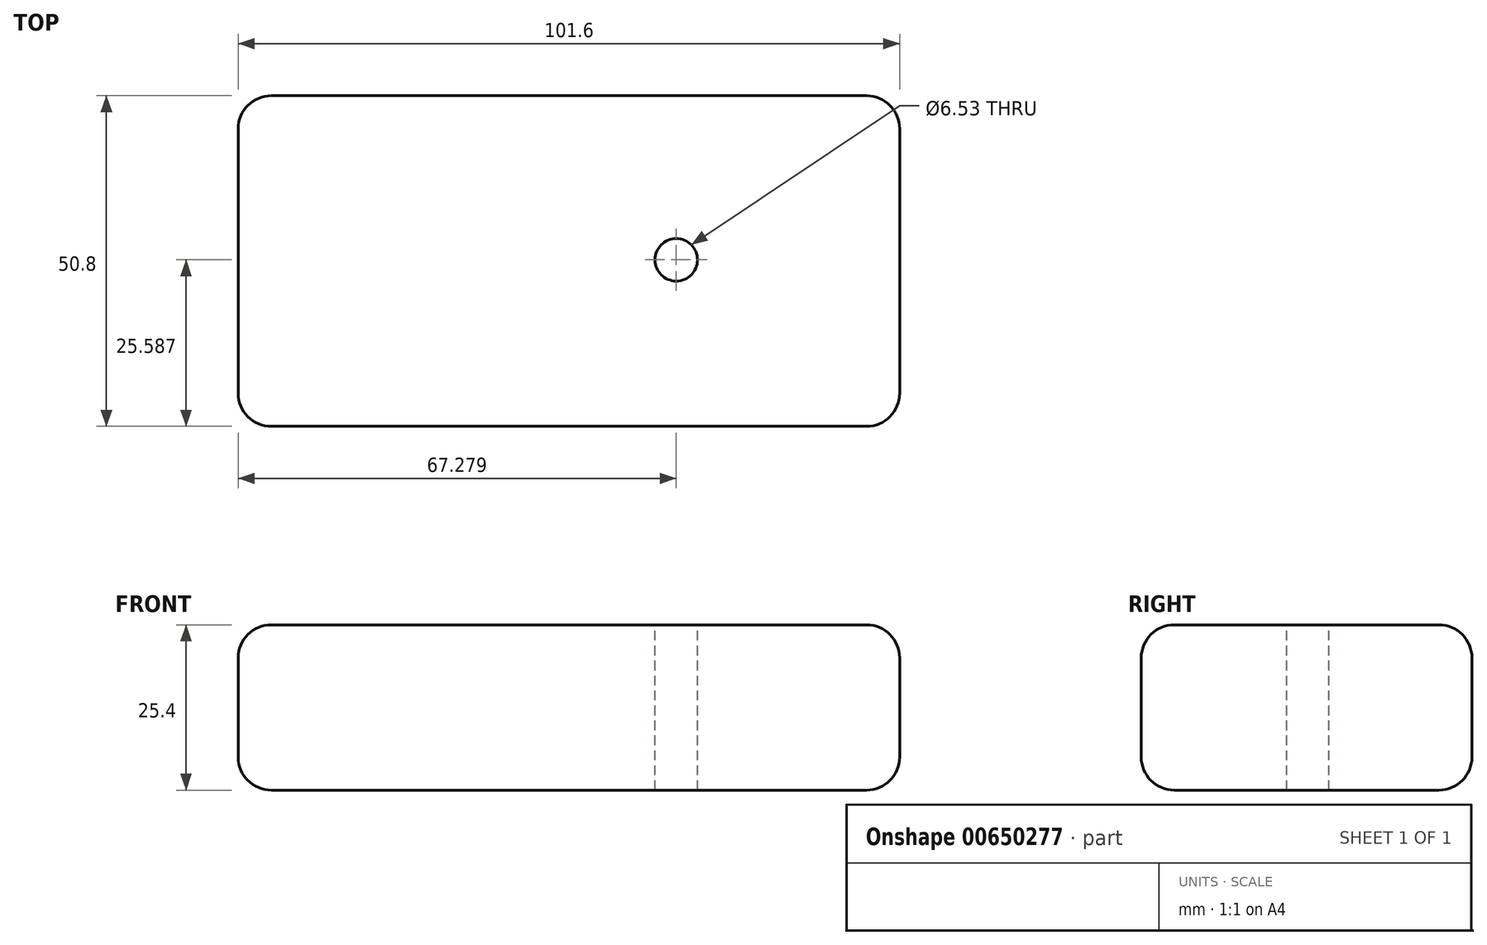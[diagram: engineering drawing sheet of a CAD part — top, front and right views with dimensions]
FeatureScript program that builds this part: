
annotation { "Feature Type Name" : "Feature", "Feature Type Description" : "" }
export const myFeature = defineFeature(function(context is Context, id is Id, definition is map)
    precondition{}
    {
        {
            var Q0;
            Q0=qCreatedBy(makeId("Top.planeOp"),FACE);
            var sketch = newSketch(context, id + "F0", { "sketchPlane" : qUnion([Q0])});
            skLineSegment(sketch, "E0.bottom", {"start": v(0, 50.8) * mm, "end": v(101.6, 50.8) * mm});
            skLineSegment(sketch, "E0.top", {"start": v(0, 0) * mm, "end": v(101.6, 0) * mm});
            skLineSegment(sketch, "E0.left", {"start": v(0, 50.8) * mm, "end": v(0, 0) * mm});
            skLineSegment(sketch, "E0.right", {"start": v(101.6, 50.8) * mm, "end": v(101.6, 0) * mm});
            skSolve(sketch);
        }
        {
            var Q0;
            Q0 = qSketchRegion(id + "F0", true);
            extrude(context, id + "F1", {"entities" : qUnion([Q0]), "depth" : 25.4 * mm, "offsetDistance" : 25.4 * mm});
        }
        {
            var Q0;
            Q0=makeQuery(id+"F1.opExtrude","CAP_FACE",FACE,{"disambiguationData":[OSD([sQuery(id+"F0.wireOp",EDGE,"E0.bottom"),sQuery(id+"F0.wireOp",EDGE,"E0.top"),sQuery(id+"F0.wireOp",EDGE,"E0.left"),sQuery(id+"F0.wireOp",EDGE,"E0.right")])],"isStart":false});
            var sketch = newSketch(context, id + "F2", { "sketchPlane" : qUnion([Q0])});
            skPoint(sketch, "E1", {"position": v(67.28, 25.59) * mm});
            skSolve(sketch);
        }
        {
            var Q0;
            Q0=sQuery(id+"F2.wireOp",VERTEX,"E1");
            var Q1;
            Q1=makeQuery(id+"F1.opExtrude","SWEPT_BODY",BODY,{"disambiguationData":[OSD([sQuery(id+"F0.wireOp",EDGE,"E0.bottom"),sQuery(id+"F0.wireOp",EDGE,"E0.top"),sQuery(id+"F0.wireOp",EDGE,"E0.left"),sQuery(id+"F0.wireOp",EDGE,"E0.right")])]});
            hole(context, id + "F3", {"style" : HoleStyle.SIMPLE, "endStyle" : HoleEndStyle.THROUGH, "standardTappedOrClearance" : lookupTablePath({ "standard" : "ANSI", "fit" : "Close", "size" : "1/4", "type" : "Clearance" }), "standardBlindInLast" : lookupTablePath({ "fit" : "Close", "standard" : "ANSI", "size" : "1/4", "type" : "Clearance" }), "holeDiameter" : 6.53 * mm, "majorDiameter" : 6.35 * mm, "isTappedThrough" : true, "tappedDepth" : 12.7 * mm, "tapClearance" : 3, "locations" : qUnion([Q0]), "scope" : qUnion([Q1])});
        }
        {
            var Q0;
            Q0=makeQuery(id+"F1.opExtrude","SWEPT_EDGE",EDGE,{"disambiguationData":[OSD([sQuery(id+"F0.wireOp",EDGE,"E0.bottom"),sQuery(id+"F0.wireOp",EDGE,"E0.right")])]});
            var Q1;
            Q1=makeQuery(id+"F1.opExtrude","SWEPT_EDGE",EDGE,{"disambiguationData":[OSD([sQuery(id+"F0.wireOp",EDGE,"E0.top"),sQuery(id+"F0.wireOp",EDGE,"E0.right")])]});
            var Q2;
            Q2=makeQuery(id+"F1.opExtrude","SWEPT_EDGE",EDGE,{"disambiguationData":[OSD([sQuery(id+"F0.wireOp",EDGE,"E0.top"),sQuery(id+"F0.wireOp",EDGE,"E0.left")])]});
            var Q3;
            Q3=makeQuery(id+"F1.opExtrude","SWEPT_EDGE",EDGE,{"disambiguationData":[OSD([sQuery(id+"F0.wireOp",EDGE,"E0.bottom"),sQuery(id+"F0.wireOp",EDGE,"E0.left")])]});
            fillet(context, id + "F4", {"entities" : qUnion([Q0, Q1, Q2, Q3]), "radius" : 5.08 * mm, "tangentPropagation" : true, "allowEdgeOverflow" : false});
        }
        {
            var Q0;
            Q0=makeQuery(id+"F1.opExtrude","CAP_EDGE",EDGE,{"disambiguationData":[OSD([sQuery(id+"F0.wireOp",EDGE,"E0.right")])],"isStart":false});
            fillet(context, id + "F5", {"entities" : qUnion([Q0]), "radius" : 5.08 * mm, "tangentPropagation" : true, "allowEdgeOverflow" : false});
        }
        {
            var Q0;
            Q0=makeQuery(id+"F1.opExtrude","CAP_EDGE",EDGE,{"disambiguationData":[OSD([sQuery(id+"F0.wireOp",EDGE,"E0.right")])],"isStart":true});
            fillet(context, id + "F6", {"entities" : qUnion([Q0]), "radius" : 5.08 * mm, "tangentPropagation" : true, "allowEdgeOverflow" : false});
        }
    });
